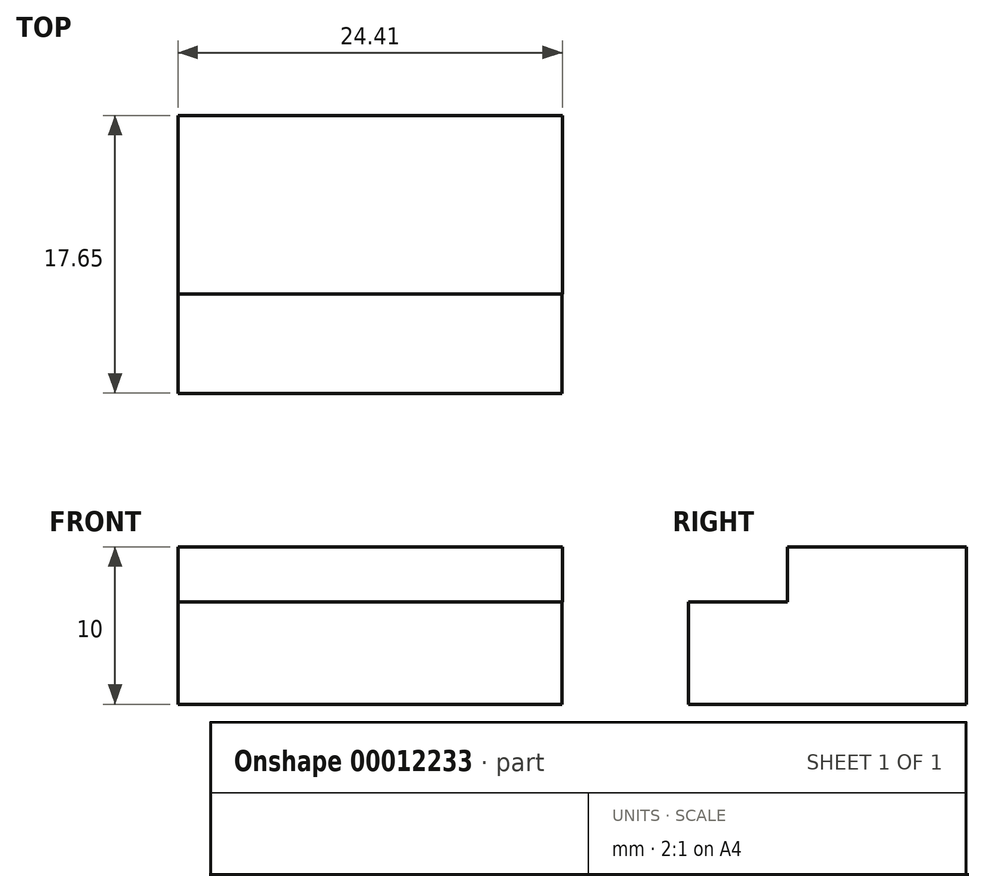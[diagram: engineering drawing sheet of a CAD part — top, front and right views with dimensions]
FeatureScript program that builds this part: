
annotation { "Feature Type Name" : "Feature", "Feature Type Description" : "" }
export const myFeature = defineFeature(function(context is Context, id is Id, definition is map)
    precondition{}
    {
        {
            var Q0;
            Q0=qCreatedBy(makeId("Top.planeOp"),FACE);
            var sketch = newSketch(context, id + "F0", { "sketchPlane" : qUnion([Q0])});
            skText(sketch, "E0", { "text": "-", "fontName": "OpenSans-Bold.ttf"});
            const initialGuessF0  = {"E0": [-0.0332, 0, 1, 0, 0.067]};
            skSetInitialGuess(sketch, initialGuessF0);
            skSolve(sketch);
        }
        {
            var Q0;
            Q0=makeQuery(id+"F0.imprint","IMPRINT",FACE,{"disambiguationData":[TD([[makeQuery(id+"F0.imprint","IMPRINT",EDGE,{"derivedFrom":sQuery(id+"F0.wireOp",EDGE,"E0.sketch_text.stroke-0")}),-1.0]])]});
            extrude(context, id + "F1", {"entities" : qUnion([Q0]), "depth" : 10 * mm});
        }
        {
            var Q0;
            Q0=makeQuery(id+"F1.opExtrude","SWEPT_FACE",FACE,{"disambiguationData":[OSD([sQuery(id+"F0.wireOp",EDGE,"E0.sketch_text.stroke-3")])]});
            var sketch = newSketch(context, id + "F2", { "sketchPlane" : qUnion([Q0])});
            skLineSegment(sketch, "E1.bottom", {"start": v(-30.43, 0) * mm, "end": v(-6.03, 0) * mm});
            skLineSegment(sketch, "E1.top", {"start": v(-30.43, 6.5) * mm, "end": v(-6.03, 6.5) * mm});
            skLineSegment(sketch, "E1.left", {"start": v(-30.43, 0) * mm, "end": v(-30.43, 6.5) * mm});
            skLineSegment(sketch, "E1.right", {"start": v(-6.03, 0) * mm, "end": v(-6.03, 6.5) * mm});
            skSolve(sketch);
        }
        {
            var Q0;
            Q0 = qSketchRegion(id + "F2", true);
            extrude(context, id + "F3", {"entities" : qUnion([Q0]), "operationType" : NewBodyOperationType.ADD, "depth" : 6.3 * mm});
        }
    });
